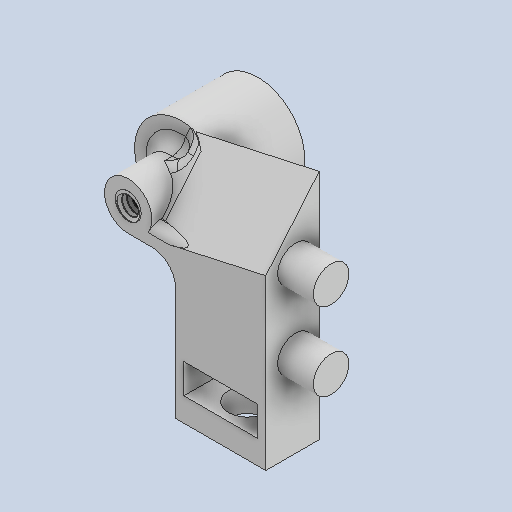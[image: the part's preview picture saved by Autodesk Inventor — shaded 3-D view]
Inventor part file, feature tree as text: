
AUTODESK INVENTOR PART (.ipt)
format: ipt  version: 2022.2 (Build 262287000, 287)  size: 1,413,632 bytes
history: native  units: mm
features: sketch x8, extrude x7, fillet x7, projected_geometry x5, other x4, draft x2, reference x2, plane x1, chamfer x1, hole x1, thread x1, revolve x1, helix x1
ambient origin geometry x8: Origin, YZ Plane, XZ Plane, XY Plane, X Axis, Y Axis, Z Axis, Center Point
bodies: Solid1 (feature_tree), Solid3 (feature_tree)
feature tree (41):
  extrude  "Extrusion1"  Depth=1.5mm TaperAngle=0.0deg
  fillet  "Fillet1"  Radius=2.0mm
  fillet  "Fillet2"  Radius=0.3mm
  sketch  "Sketch2"  dims[d0=2.2mm d10=1.5mm d11=0.0mm d15=2.0mm d16=0.3mm]
  extrude  "Extrusion4"  Depth=2.0mm TaperAngle=0.0deg
  extrude  "Extrusion5"  Depth=2.0mm TaperAngle=0.0deg
  draft  "FaceDraft4"
  fillet  "Fillet10"  Radius=3.0mm
  sketch  "Sketch8"  dims[d48=7.92mm d49=2.0mm d50=0.0mm d52=3.0mm]
  plane  "Work Plane1"
  extrude  "Extrusion6"  Depth=2.0mm
  extrude  "Extrusion7"  Depth=0.75mm
  chamfer  "Chamfer6"  Distance=1.99mm Angle=45.0deg
  draft  "FaceDraft5"
  fillet  "Fillet12"  Radius=1.116107mm
  fillet  "Fillet13"  Radius=9.599311mm
  extrude  "Extrusion8"  Depth=2.5mm
  fillet  "Fillet14"  Radius=0.7mm
  extrude  "Extrusion9"  Depth=7.0mm
  hole  "Hole1"  [1 undecoded]
  thread  "Thread2"  [1 undecoded]
  revolve  "Revolution2"  [1 undecoded]
  helix  "Coil2"  [1 undecoded]
  fillet  "Fillet15"  Radius=2.0mm
  projected_geometry  "Projected Loop2"
  projected_geometry  "Projected Loop3"
  sketch  "Sketch7"  dims[d23=3.0mm d24=0.0mm d44=2.0mm d45=0.0mm]
  projected_geometry  "Projected Loop4"
  sketch  "Sketch9"  dims[d53=3.0mm d54=0.0mm d57=2.0mm]
  reference  "Reference8"
  projected_geometry  "Projected Loop5"
  sketch  "Sketch13"  dims[d58=6.981317mm d59=0.75mm d61=1.99mm d62=1.0mm d63=45.0deg d66=1.116107mm d68=2.568591mm d76=9.599311mm]
  reference  "Reference9"
  sketch  "Sketch14"  dims[d88=6.2mm d89=2.5mm d90=0.7mm]
  projected_geometry  "Projected Loop6"
  sketch  "Sketch15"  dims[d91=0.7mm d92=7.0mm]
  sketch  "Sketch16"  dims[d94=2.0mm d95=3.0mm d96=5.0mm d97=0.5mm d98=-15.706218mm d99=2.0mm d103=1.0mm d104=0.0mm d105=0.0mm d106=1.0mm d107=3.2mm d108=9.5mm d109=0.0mm d110=2.18mm d111=6.0mm d112=6.0mm d113=4.0mm d114=90.0deg d115=8.0mm d116=20.594885mm d117=10.9mm d118=0.0mm d119=9.599311mm d120=0.064033mm d121=0.064033mm d124=0.4mm d126=9.599311mm d128=0.0mm d129=0.4004mm d130=11.7mm d131=10.0mm d132=0.0mm d133=0.0mm d134=0.0mm d135=0.0mm d136=0.0mm d137=1.0mm d36=0.5mm d37=0.872665mm d38=0.5mm d39=0.872665mm]
  other  "<userpath>\Documents\Inventor\Wire Bender\Assembly.iam"
  other  "Assembly.iam"
  other  "Crank:1"
  other  "Bending Base:1"
note: 4 required parameter values undecoded (feature->parameter linkage not recoverable at this tier; creation-order binding heuristic only, values carry confidence <= 0.55)